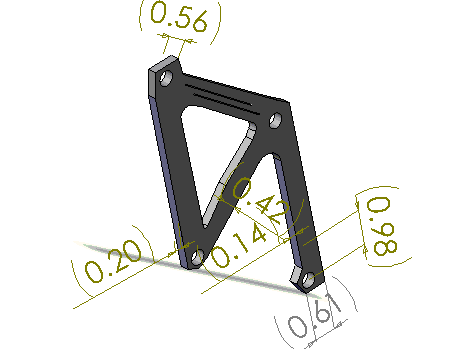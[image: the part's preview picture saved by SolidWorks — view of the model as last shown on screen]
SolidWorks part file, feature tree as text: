
SOLIDWORKS PART (.sldprt)
format: sldprt  version: not decoded by parser v0  size: 724,992 bytes
history: native  units: mm
features: sketch x445, extrude x1 + 10 further entries (+9 scaffold rows collapsed; 39 parser-record rows omitted)
feature tree (504):
  "Annotations"  RD1=14.283299mm
  scaffold x9  (default folders/planes/origin — collapsed)
  sketch  "Sketch1"  dims[c1.D4=~5.100466mm c1.D10=10.16mm c1.D15=6.35mm c1.D17=5.08mm c1.D18=5.08mm c1.D2=2.54mm c1.D19=8.255mm c2.D10=3.81mm c2.D15=3.81mm c2.D17=2.54mm c3.D10=45.72mm c3.D15=12.7mm c3.D17=81.28mm c4.D10=6.35mm c4.D16=6.35mm c4.D15=6.35mm c4.D17=~42.135374mm c5.D15=5.08mm c5.D1=12.7mm c5.D2=12.7mm c5.D3=~92.622632mm c6.D3=~45.206971deg c7.D3=~785.398163mm c7.D4=101.6mm c7.D5=12.7mm c7.D6=12.7mm c7.D7=6.35mm c7.D8=76.2mm c7.D9=91.44mm c7.D10=6.35mm c7.D11=88.9mm c7.D12=120.65mm c7.D13=20.32mm c8.D10=~104.652849mm c9.D10=~55.604689mm c10.D10=~104.652849mm c11.D10=~6283.185307mm c11.D14=6.35mm c11.D16=6.35mm c11.D20=15.24mm c11.D21=12.7mm c11.D22=7.62mm c11.D23=7.62mm c12.D16=7.62mm c12.D18=8.128mm c12.D24=3.556mm c12.D25=5.08mm c13.D16=~70.817007mm c14.D16=~3117.473443mm c15.D16=2.54mm c16.D16=~1570.796327mm c17.D16=1.27mm c17.D17=0.635mm c17.D18=0.635mm]
  extrude  "Extrude2"  Depth=6.35mm cosMaterialEX=69000000000.0
  sketch  "cosMaterialNUXY"
  sketch  "cosMaterialGXY"
  sketch  "cosMaterialALPX"
  sketch  "cosMaterialDENS"
  sketch  "cosMaterialKX"
  sketch  "cosMaterialC"
  sketch  "Units"
  sketch  "AnalysisType"
  sketch  "MeshType"
  sketch  "cosMaterialSIGYLD"
  sketch  "cosMaterialSIGXT"
  sketch  "cosMaterialSIGXC"  dims[sMaterialName=0.0deg cosFMVItemName=0.0deg cosMaterialName=0.0deg cosComponentName=0.0deg]
  sketch  "cosMaterialModel"
  sketch  "cosMaterialEY"
  sketch  "cosMaterialEZ"
  sketch  "cosMaterialNUXZ"
  sketch  "cosMaterialNUYZ"
  sketch  "cosMaterialGXZ"
  sketch  "cosMaterialGYZ"
  sketch  "cosMaterialALPY"
  sketch  "cosMaterialALPZ"
  sketch  "cosMaterialKY"
  sketch  "cosMaterialKZ"  dims[cosMaterialType=0.0deg cosMaterialLibFile=0.0deg cosMaterialRefPlaneName=0.0deg]
  sketch  "cosMaterialSource"
  sketch  "cosMaterialEX"
  sketch  "cosMaterialNUXY"
  sketch  "cosMaterialGXY"
  sketch  "cosMaterialALPX"
  sketch  "cosMaterialDENS"
  sketch  "cosMaterialKX"
  sketch  "cosMaterialC"
  sketch  "Units"
  sketch  "AnalysisType"
  sketch  "MeshType"
  sketch  "cosMaterialSIGYLD"
  sketch  "cosMaterialSIGXT"
  sketch  "cosMaterialSIGXC"  dims[sMaterialSourceName=0.0deg sMaterialName=0.0deg cosFMVItemName=0.0deg cosMaterialName=0.0deg cosComponentName=0.0deg]
  sketch  "cosMaterialModel"
  sketch  "cosMaterialEY"
  sketch  "cosMaterialEZ"
  sketch  "cosMaterialNUXZ"
  sketch  "cosMaterialNUYZ"
  sketch  "cosMaterialGXZ"
  sketch  "cosMaterialGYZ"
  sketch  "cosMaterialALPY"
  sketch  "cosMaterialALPZ"
  sketch  "cosMaterialKY"
  sketch  "cosMaterialKZ"  dims[cosMaterialType=0.0deg cosMaterialLibFile=0.0deg cosMaterialRefPlaneName=0.0deg]
  sketch  "cosMaterialSource"
  "Stress Test:Restraint-3"
  sketch  "RestraintType"
  sketch  "Value"
  sketch  "cosRestraintComp:1"
  sketch  "cosRestraintComp:2"
  sketch  "cosRestraintComp:3"
  sketch  "cosRestraintComp:4"
  sketch  "cosRestraintComp:5"
  sketch  "cosRestraintComp:6"
  sketch  "Unit"
  sketch  "AnalysisType"
  sketch  "MeshType"
  sketch  "cosRestraintCompCheck1"
  sketch  "cosRestraintCompCheck2"
  sketch  "cosRestraintCompCheck3"
  sketch  "cosRestraintCompCheck4"
  sketch  "cosRestraintCompCheck5"
  sketch  "cosRestraintCompCheck6"
  sketch  "cosRestraintRefPlaneSet"
  sketch  "cosRestraintRefPlaneOrigin1"
  sketch  "cosRestraintRefPlaneOrigin2"
  sketch  "cosRestraintRefPlaneOrigin3"
  sketch  "cosRestraintRefPlaneXDir1"
  sketch  "cosRestraintRefPlaneXDir2"
  sketch  "cosRestraintRefPlaneXDir3"
  sketch  "cosRestraintRefPlaneNormal1"
  sketch  "cosRestraintRefPlaneNormal2"
  sketch  "cosRestraintRefPlaneNormal3"  dims[cosRestraintRefPlaneName=0.0deg]
  sketch  "cosRestraintCoordSystemType"
  sketch  "cosRestraintFaceTypeMask"  dims[cosFMVItemName=0.0deg cosLBCSymbolColor=0.0deg]
  sketch  "cosLBCState"  dims[cosRestraint7=0.0]
  sketch  "RestraintType"
  sketch  "Value"
  sketch  "cosRestraintComp:1"
  sketch  "cosRestraintComp:2"
  sketch  "cosRestraintComp:3"
  sketch  "cosRestraintComp:4"
  sketch  "cosRestraintComp:5"
  sketch  "cosRestraintComp:6"
  sketch  "Unit"
  sketch  "AnalysisType"
  sketch  "MeshType"
  sketch  "cosRestraintCompCheck1"
  sketch  "cosRestraintCompCheck2"
  sketch  "cosRestraintCompCheck3"
  sketch  "cosRestraintCompCheck4"
  sketch  "cosRestraintCompCheck5"
  sketch  "cosRestraintCompCheck6"
  sketch  "cosRestraintRefPlaneSet"
  sketch  "cosRestraintRefPlaneOrigin1"
  sketch  "cosRestraintRefPlaneOrigin2"
  sketch  "cosRestraintRefPlaneOrigin3"
  sketch  "cosRestraintRefPlaneXDir1"
  sketch  "cosRestraintRefPlaneXDir2"
  sketch  "cosRestraintRefPlaneXDir3"
  sketch  "cosRestraintRefPlaneNormal1"
  sketch  "cosRestraintRefPlaneNormal2"
  sketch  "cosRestraintRefPlaneNormal3"  dims[cosRestraintRefPlaneName=0.0deg]
  sketch  "cosRestraintCoordSystemType"
  sketch  "cosRestraintFaceTypeMask"  dims[cosFMVItemName=0.0deg cosLBCSymbolColor=0.0deg]
  sketch  "cosLBCState"
  "Stress Test:Restraint-4"
  sketch  "RestraintType"
  sketch  "Value"
  sketch  "cosRestraintComp:1"
  sketch  "cosRestraintComp:2"
  sketch  "cosRestraintComp:3"
  sketch  "cosRestraintComp:4"
  sketch  "cosRestraintComp:5"
  sketch  "cosRestraintComp:6"
  sketch  "Unit"
  sketch  "AnalysisType"
  sketch  "MeshType"
  sketch  "cosRestraintCompCheck1"
  sketch  "cosRestraintCompCheck2"
  sketch  "cosRestraintCompCheck3"
  sketch  "cosRestraintCompCheck4"
  sketch  "cosRestraintCompCheck5"
  sketch  "cosRestraintCompCheck6"
  sketch  "cosRestraintRefPlaneSet"
  sketch  "cosRestraintRefPlaneOrigin1"
  sketch  "cosRestraintRefPlaneOrigin2"
  sketch  "cosRestraintRefPlaneOrigin3"
  sketch  "cosRestraintRefPlaneXDir1"
  sketch  "cosRestraintRefPlaneXDir2"
  sketch  "cosRestraintRefPlaneXDir3"
  sketch  "cosRestraintRefPlaneNormal1"
  sketch  "cosRestraintRefPlaneNormal2"
  sketch  "cosRestraintRefPlaneNormal3"  dims[cosRestraintRefPlaneName=0.0deg]
  sketch  "cosRestraintCoordSystemType"
  sketch  "cosRestraintFaceTypeMask"  dims[cosFMVItemName=0.0deg cosLBCSymbolColor=0.0deg]
  sketch  "cosLBCState"
  "Stress Test:Force-3"
  sketch  "cosForceComp:1"
  sketch  "cosForceComp:2"
  sketch  "cosForceComp:3"
  sketch  "cosForceComp:4"
  sketch  "cosForceComp:5"
  sketch  "cosForceComp:6"
  sketch  "cosForceTorqueNF"
  sketch  "cosForceCompCheck1"
  sketch  "cosForceCompCheck2"
  sketch  "cosForceCompCheck3"
  sketch  "cosForceCompCheck4"
  sketch  "cosForceCompCheck5"
  sketch  "cosForceCompCheck6"
  sketch  "Unit"
  sketch  "AnalysisType"
  sketch  "MeshType"
  sketch  "cosForceRefPlaneSet"
  sketch  "cosForceRefPlaneOrigin1"
  sketch  "cosForceRefPlaneOrigin2"
  sketch  "cosForceRefPlaneOrigin3"
  sketch  "cosForceRefPlaneXDir1"
  sketch  "cosForceRefPlaneXDir2"
  sketch  "cosForceRefPlaneXDir3"
  sketch  "cosForceRefPlaneNormal1"
  sketch  "cosForceRefPlaneNormal2"
  sketch  "cosForceRefPlaneNormal3"  dims[cosForceRefPlaneName=0.0deg]
  sketch  "cosForceCoordSystemType"
  sketch  "cosForceType"  dims[cosFMVItemName=0.0deg]
  sketch  "cosDistributionType"  dims[cosDistributionCoordSysName=0.0deg]
  sketch  "cosDistributionCoef1"
  sketch  "cosDistributionCoef2"
  sketch  "cosDistributionCoef3"
  sketch  "cosDistributionCoef4"
  sketch  "cosDistributionCoef5"
  sketch  "cosDistributionCoef6"  dims[cosLBCSymbolColor=0.0deg]
  sketch  "cosLBCState"  dims[cosForce7=0.0]
  sketch  "cosForceComp:1"
  sketch  "cosForceComp:2"
  sketch  "cosForceComp:3"
  sketch  "cosForceComp:4"
  sketch  "cosForceComp:5"
  sketch  "cosForceComp:6"
  sketch  "cosForceTorqueNF"
  sketch  "cosForceCompCheck1"
  sketch  "cosForceCompCheck2"
  sketch  "cosForceCompCheck3"
  sketch  "cosForceCompCheck4"
  sketch  "cosForceCompCheck5"
  sketch  "cosForceCompCheck6"
  sketch  "Unit"
  sketch  "AnalysisType"
  sketch  "MeshType"
  sketch  "cosForceRefPlaneSet"
  sketch  "cosForceRefPlaneOrigin1"
  sketch  "cosForceRefPlaneOrigin2"
  sketch  "cosForceRefPlaneOrigin3"
  sketch  "cosForceRefPlaneXDir1"
  sketch  "cosForceRefPlaneXDir2"
  sketch  "cosForceRefPlaneXDir3"
  sketch  "cosForceRefPlaneNormal1"
  sketch  "cosForceRefPlaneNormal2"
  sketch  "cosForceRefPlaneNormal3"  dims[cosForceRefPlaneName=0.0deg]
  sketch  "cosForceCoordSystemType"
  sketch  "cosForceType"  dims[cosFMVItemName=0.0deg]
  sketch  "cosDistributionType"  dims[cosDistributionCoordSysName=0.0deg]
  sketch  "cosDistributionCoef1"
  sketch  "cosDistributionCoef2"
  sketch  "cosDistributionCoef3"
  sketch  "cosDistributionCoef4"
  sketch  "cosDistributionCoef5"
  sketch  "cosDistributionCoef6"  dims[cosLBCSymbolColor=0.0deg]
  sketch  "cosLBCState"
  "Stress Test:Force-4"
  sketch  "cosForceComp:1"
  sketch  "cosForceComp:2"
  sketch  "cosForceComp:3"
  sketch  "cosForceComp:4"
  sketch  "cosForceComp:5"
  sketch  "cosForceComp:6"
  sketch  "cosForceTorqueNF"
  sketch  "cosForceCompCheck1"
  sketch  "cosForceCompCheck2"
  sketch  "cosForceCompCheck3"
  sketch  "cosForceCompCheck4"
  sketch  "cosForceCompCheck5"
  sketch  "cosForceCompCheck6"
  sketch  "Unit"
  sketch  "AnalysisType"
  sketch  "MeshType"
  sketch  "cosForceRefPlaneSet"
  sketch  "cosForceRefPlaneOrigin1"
  sketch  "cosForceRefPlaneOrigin2"
  sketch  "cosForceRefPlaneOrigin3"
  sketch  "cosForceRefPlaneXDir1"
  sketch  "cosForceRefPlaneXDir2"
  sketch  "cosForceRefPlaneXDir3"
  sketch  "cosForceRefPlaneNormal1"
  sketch  "cosForceRefPlaneNormal2"
  sketch  "cosForceRefPlaneNormal3"  dims[cosForceRefPlaneName=0.0deg]
  sketch  "cosForceCoordSystemType"
  sketch  "cosForceType"  dims[cosFMVItemName=0.0deg]
  sketch  "cosDistributionType"  dims[cosDistributionCoordSysName=0.0deg]
  sketch  "cosDistributionCoef1"
  sketch  "cosDistributionCoef2"
  sketch  "cosDistributionCoef3"
  sketch  "cosDistributionCoef4"
  sketch  "cosDistributionCoef5"
  sketch  "cosDistributionCoef6"  dims[cosLBCSymbolColor=0.0deg]
  sketch  "cosLBCState"
  "freq:Material-1"
  sketch  "cosMaterialEX"
  sketch  "cosMaterialNUXY"
  sketch  "cosMaterialGXY"
  sketch  "cosMaterialALPX"
  sketch  "cosMaterialDENS"
  sketch  "cosMaterialKX"
  sketch  "cosMaterialC"
  sketch  "Units"
  sketch  "AnalysisType"
  sketch  "MeshType"
  sketch  "cosMaterialSIGYLD"
  sketch  "cosMaterialSIGXT"
  sketch  "cosMaterialSIGXC"  dims[sMaterialSourceName=0.0deg sMaterialName=0.0deg cosFMVItemName=0.0deg cosMaterialName=0.0deg cosComponentName=0.0deg]
  sketch  "cosMaterialModel"
  sketch  "cosMaterialEY"
  sketch  "cosMaterialEZ"
  sketch  "cosMaterialNUXZ"
  sketch  "cosMaterialNUYZ"
  sketch  "cosMaterialGXZ"
  sketch  "cosMaterialGYZ"
  sketch  "cosMaterialALPY"
  sketch  "cosMaterialALPZ"
  sketch  "cosMaterialKY"
  sketch  "cosMaterialKZ"  dims[cosMaterialType=0.0deg cosMaterialLibFile=0.0deg cosMaterialRefPlaneName=0.0deg]
  sketch  "cosMaterialSource"
  "freq:Restraint-1"
  sketch  "RestraintType"
  sketch  "Value"
  sketch  "cosRestraintComp:1"
  sketch  "cosRestraintComp:2"
  sketch  "cosRestraintComp:3"
  sketch  "cosRestraintComp:4"
  sketch  "cosRestraintComp:5"
  sketch  "cosRestraintComp:6"
  sketch  "Unit"
  sketch  "AnalysisType"
  sketch  "MeshType"
  sketch  "cosRestraintCompCheck1"
  sketch  "cosRestraintCompCheck2"
  sketch  "cosRestraintCompCheck3"
  sketch  "cosRestraintCompCheck4"
  sketch  "cosRestraintCompCheck5"
  sketch  "cosRestraintCompCheck6"
  sketch  "cosRestraintRefPlaneSet"
  sketch  "cosRestraintRefPlaneOrigin1"
  sketch  "cosRestraintRefPlaneOrigin2"
  sketch  "cosRestraintRefPlaneOrigin3"
  sketch  "cosRestraintRefPlaneXDir1"
  sketch  "cosRestraintRefPlaneXDir2"
  sketch  "cosRestraintRefPlaneXDir3"
  sketch  "cosRestraintRefPlaneNormal1"
  sketch  "cosRestraintRefPlaneNormal2"
  sketch  "cosRestraintRefPlaneNormal3"  dims[cosRestraintRefPlaneName=0.0deg]
  sketch  "cosRestraintCoordSystemType"
  sketch  "cosRestraintFaceTypeMask"  dims[cosFMVItemName=0.0deg cosLBCSymbolColor=0.0deg]
  sketch  "cosLBCState"
  "freq:Restraint-2"
  sketch  "RestraintType"
  sketch  "Value"
  sketch  "cosRestraintComp:1"
  sketch  "cosRestraintComp:2"
  sketch  "cosRestraintComp:3"
  sketch  "cosRestraintComp:4"
  sketch  "cosRestraintComp:5"
  sketch  "cosRestraintComp:6"
  sketch  "Unit"
  sketch  "AnalysisType"
  sketch  "MeshType"
  sketch  "cosRestraintCompCheck1"
  sketch  "cosRestraintCompCheck2"
  sketch  "cosRestraintCompCheck3"
  sketch  "cosRestraintCompCheck4"
  sketch  "cosRestraintCompCheck5"
  sketch  "cosRestraintCompCheck6"
  sketch  "cosRestraintRefPlaneSet"
  sketch  "cosRestraintRefPlaneOrigin1"
  sketch  "cosRestraintRefPlaneOrigin2"
  sketch  "cosRestraintRefPlaneOrigin3"
  sketch  "cosRestraintRefPlaneXDir1"
  sketch  "cosRestraintRefPlaneXDir2"
  sketch  "cosRestraintRefPlaneXDir3"
  sketch  "cosRestraintRefPlaneNormal1"
  sketch  "cosRestraintRefPlaneNormal2"
  sketch  "cosRestraintRefPlaneNormal3"  dims[cosRestraintRefPlaneName=0.0deg]
  sketch  "cosRestraintCoordSystemType"
  sketch  "cosRestraintFaceTypeMask"  dims[cosFMVItemName=0.0deg cosLBCSymbolColor=0.0deg]
  sketch  "cosLBCState"
  "freq:Force-1"
  sketch  "cosForceComp:1"
  sketch  "cosForceComp:2"
  sketch  "cosForceComp:3"
  sketch  "cosForceComp:4"
  sketch  "cosForceComp:5"
  sketch  "cosForceComp:6"
  sketch  "cosForceTorqueNF"
  sketch  "cosForceCompCheck1"
  sketch  "cosForceCompCheck2"
  sketch  "cosForceCompCheck3"
  sketch  "cosForceCompCheck4"
  sketch  "cosForceCompCheck5"
  sketch  "cosForceCompCheck6"
  sketch  "Unit"
  sketch  "AnalysisType"
  sketch  "MeshType"
  sketch  "cosForceRefPlaneSet"
  sketch  "cosForceRefPlaneOrigin1"
  sketch  "cosForceRefPlaneOrigin2"
  sketch  "cosForceRefPlaneOrigin3"
  sketch  "cosForceRefPlaneXDir1"
  sketch  "cosForceRefPlaneXDir2"
  sketch  "cosForceRefPlaneXDir3"
  sketch  "cosForceRefPlaneNormal1"
  sketch  "cosForceRefPlaneNormal2"
  sketch  "cosForceRefPlaneNormal3"  dims[cosForceRefPlaneName=0.0deg]
  sketch  "cosForceCoordSystemType"
  sketch  "cosForceType"  dims[cosFMVItemName=0.0deg]
  sketch  "cosDistributionType"  dims[cosDistributionCoordSysName=0.0deg]
  sketch  "cosDistributionCoef1"
  sketch  "cosDistributionCoef2"
  sketch  "cosDistributionCoef3"
  sketch  "cosDistributionCoef4"
  sketch  "cosDistributionCoef5"
  sketch  "cosDistributionCoef6"  dims[cosLBCSymbolColor=0.0deg]
  sketch  "cosLBCState"
  "freq:Force-2"
  sketch  "cosForceComp:1"
  sketch  "cosForceComp:2"
  sketch  "cosForceComp:3"
  sketch  "cosForceComp:4"
  sketch  "cosForceComp:5"
  sketch  "cosForceComp:6"
  sketch  "cosForceTorqueNF"
  sketch  "cosForceCompCheck1"
  sketch  "cosForceCompCheck2"
  sketch  "cosForceCompCheck3"
  sketch  "cosForceCompCheck4"
  sketch  "cosForceCompCheck5"
  sketch  "cosForceCompCheck6"
  sketch  "Unit"
  sketch  "AnalysisType"
  sketch  "MeshType"
  sketch  "cosForceRefPlaneSet"
  sketch  "cosForceRefPlaneOrigin1"
  sketch  "cosForceRefPlaneOrigin2"
  sketch  "cosForceRefPlaneOrigin3"
  sketch  "cosForceRefPlaneXDir1"
  sketch  "cosForceRefPlaneXDir2"
  sketch  "cosForceRefPlaneXDir3"
  sketch  "cosForceRefPlaneNormal1"
  sketch  "cosForceRefPlaneNormal2"
  sketch  "cosForceRefPlaneNormal3"  dims[cosForceRefPlaneName=0.0deg]
  sketch  "cosForceCoordSystemType"
  sketch  "cosForceType"  dims[cosFMVItemName=0.0deg]
  sketch  "cosDistributionType"  dims[cosDistributionCoordSysName=0.0deg]
  sketch  "cosDistributionCoef1"
  sketch  "cosDistributionCoef2"
  sketch  "cosDistributionCoef3"
  sketch  "cosDistributionCoef4"
  sketch  "cosDistributionCoef5"
  sketch  "cosDistributionCoef6"  dims[cosLBCSymbolColor=0.0deg]
  sketch  "cosLBCState"
  parser-record x39  (decoder bookkeeping rows leaked as tree rows — omitted from the tree; the rows remain in map.json)
  sketch  "faceID"  dims[cosFaceID=0.0]
  sketch  "faceID"
  sketch  "faceID"
  sketch  "faceID"
  sketch  "faceID"
  sketch  "faceID"
  sketch  "faceID"
  sketch  "faceID"
  sketch  "faceID"
  sketch  "faceID"
  sketch  "faceID"
  sketch  "faceID"
  sketch  "faceID"
  sketch  "faceID"
  sketch  "faceID"
  sketch  "faceID"
  sketch  "faceID"
  sketch  "faceID"
  sketch  "faceID"
  sketch  "faceID"
  sketch  "faceID"
  sketch  "faceID"
  sketch  "faceID"
  sketch  "faceID"
  sketch  "faceID"
  sketch  "faceID"
  sketch  "faceID"
  sketch  "faceID"
  sketch  "faceID"
  sketch  "faceID"
  sketch  "faceID"
  sketch  "faceID"
  sketch  "faceID"
  sketch  "faceID"
  sketch  "faceID"
  sketch  "faceID"
  sketch  "faceID"
  sketch  "faceID"
  sketch  "faceID"
  sketch  "faceID"
decode coverage: 41 of 446 modeling features carry decoded parameters; 10 rows unclassified (native names shown)
note: ~ marks probable driven/reference dimensions
note: suppression state not decoded; provenance and decode notes live in map.json
